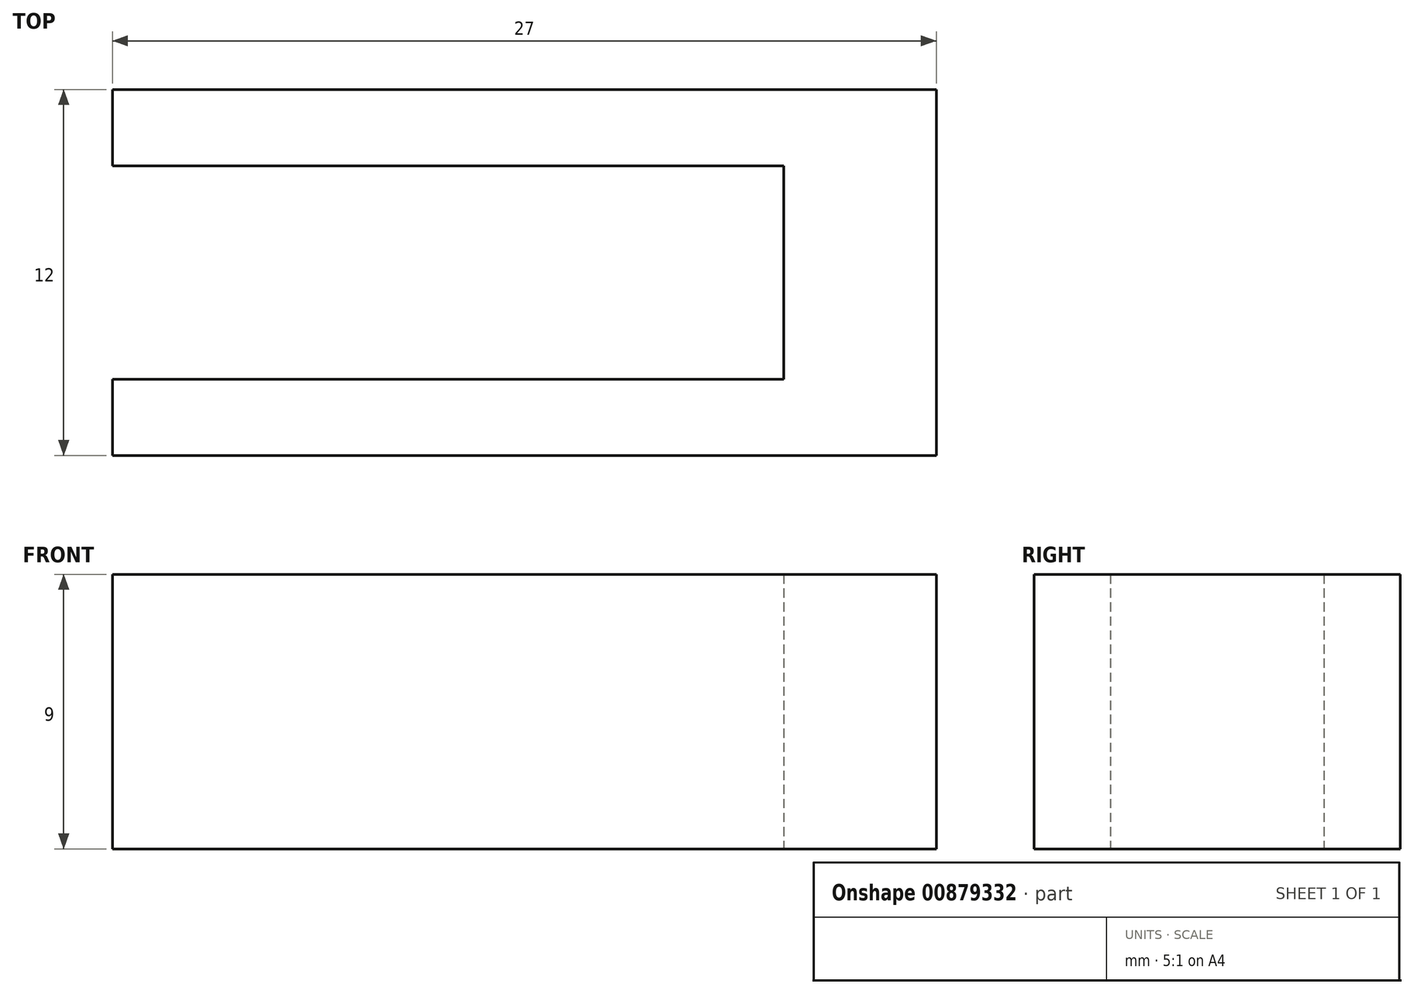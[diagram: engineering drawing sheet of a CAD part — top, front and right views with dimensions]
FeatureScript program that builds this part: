
annotation { "Feature Type Name" : "Feature", "Feature Type Description" : "" }
export const myFeature = defineFeature(function(context is Context, id is Id, definition is map)
    precondition{}
    {
        {
            var Q0;
            Q0=qCreatedBy(makeId("Top.planeOp"),FACE);
            var sketch = newSketch(context, id + "F0", { "sketchPlane" : qUnion([Q0])});
            skLineSegment(sketch, "E0.bottom", {"start": v(0, 0) * mm, "end": v(-22, 0) * mm});
            skLineSegment(sketch, "E0.top", {"start": v(0, -2.5) * mm, "end": v(-5, -2.5) * mm});
            skLineSegment(sketch, "E0.left", {"start": v(0, 0) * mm, "end": v(0, -2.5) * mm, "construction": true});
            skLineSegment(sketch, "E0.right", {"start": v(-22, 0) * mm, "end": v(-22, -2.5) * mm});
            skLineSegment(sketch, "E1", {"start": v(0, -2.5) * mm, "end": v(0, -9.5) * mm});
            skLineSegment(sketch, "E2", {"start": v(0, -9.5) * mm, "end": v(-5, -9.5) * mm});
            skLineSegment(sketch, "E3", {"start": v(-5, -9.5) * mm, "end": v(-5, -2.5) * mm, "construction": true});
            skLineSegment(sketch, "E4", {"start": v(-5, -2.5) * mm, "end": v(-22, -2.5) * mm});
            skLineSegment(sketch, "E5", {"start": v(0, -9.5) * mm, "end": v(0, -12) * mm, "construction": true});
            skLineSegment(sketch, "E6", {"start": v(-22, -12) * mm, "end": v(-22, -9.5) * mm});
            skLineSegment(sketch, "E7", {"start": v(-22, -9.5) * mm, "end": v(-5, -9.5) * mm});
            skLineSegment(sketch, "E8", {"start": v(-22, -12) * mm, "end": v(0, -12) * mm});
            skLineSegment(sketch, "E9", {"start": v(0, 0) * mm, "end": v(5, 0) * mm});
            skLineSegment(sketch, "E10", {"start": v(5, 0) * mm, "end": v(5, -12) * mm});
            skLineSegment(sketch, "E11", {"start": v(5, -12) * mm, "end": v(0, -12) * mm});
            skSolve(sketch);
        }
        {
            var Q0;
            Q0=makeQuery(id+"F0.imprint","IMPRINT",FACE,{"disambiguationData":[TD([[makeQuery(id+"F0.imprint","IMPRINT",EDGE,{"derivedFrom":sQuery(id+"F0.wireOp",EDGE,"E0.bottom")}),1.0]])]});
            extrude(context, id + "F1", {"entities" : qUnion([Q0]), "depth" : 9 * mm, "offsetDistance" : 25 * mm});
        }
    });
